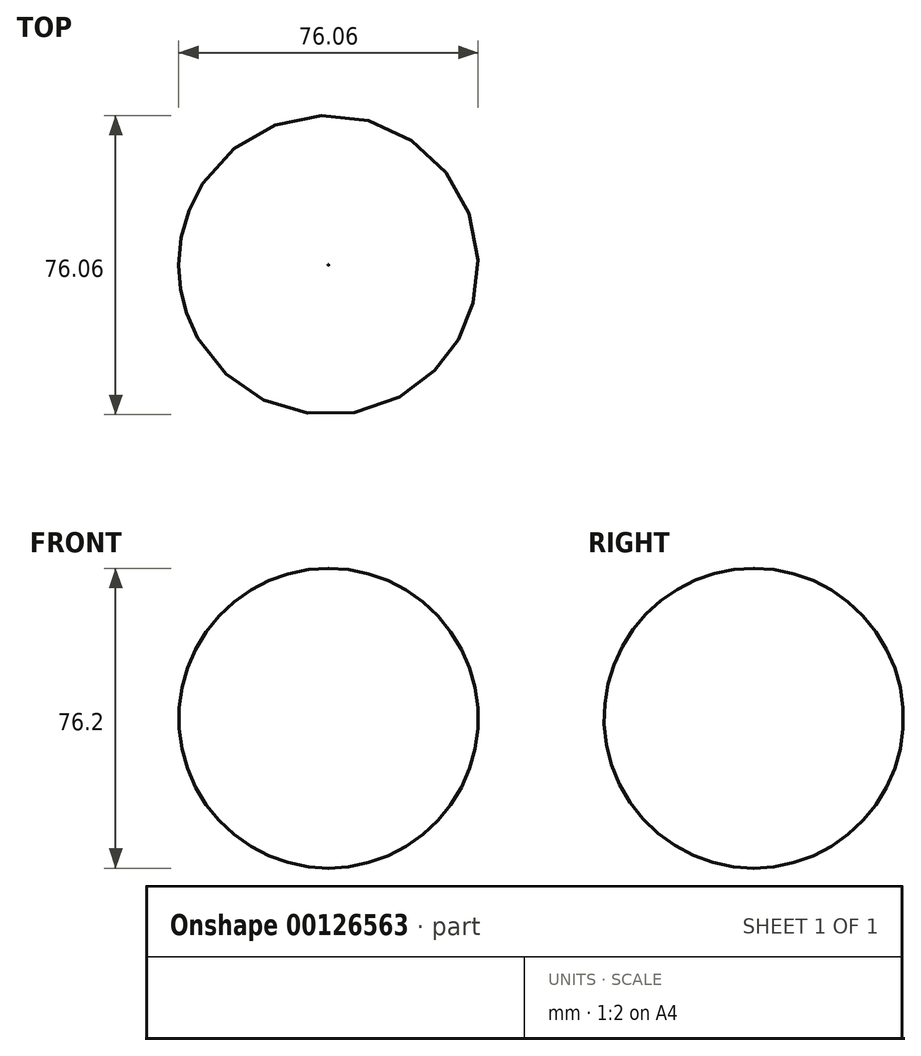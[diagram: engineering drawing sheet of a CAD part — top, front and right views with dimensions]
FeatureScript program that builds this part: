
annotation { "Feature Type Name" : "Feature", "Feature Type Description" : "" }
export const myFeature = defineFeature(function(context is Context, id is Id, definition is map)
    precondition{}
    {
        {
            var Q0;
            Q0=qCreatedBy(makeId("Top.planeOp"),FACE);
            var sketch = newSketch(context, id + "F0", { "sketchPlane" : qUnion([Q0])});
            skCircle(sketch, "E0", {"center": v(0, 0) * mm, "radius": 38.17 * mm});
            skSolve(sketch);
        }
        {
            var Q0;
            Q0=makeQuery(id+"F0.imprint","IMPRINT",FACE,{"disambiguationData":[TD([[makeQuery(id+"F0.imprint","IMPRINT",EDGE,{"derivedFrom":sQuery(id+"F0.wireOp",EDGE,"E0")}),1.0]])]});
            extrude(context, id + "F1", {"entities" : qUnion([Q0]), "oppositeDirection" : true, "depth" : 76.2 * mm});
        }
        {
            var Q0;
            Q0=makeQuery(id+"F1.opExtrude","CAP_EDGE",EDGE,{"disambiguationData":[OSD([sQuery(id+"F0.wireOp",EDGE,"E0")])],"isStart":true});
            var Q1;
            Q1=makeQuery(id+"F1.opExtrude","CAP_EDGE",EDGE,{"disambiguationData":[OSD([sQuery(id+"F0.wireOp",EDGE,"E0")])],"isStart":false});
            fillet(context, id + "F2", {"entities" : qUnion([Q0, Q1]), "radius" : 38.1 * mm, "tangentPropagation" : true, "allowEdgeOverflow" : false});
        }
    });
